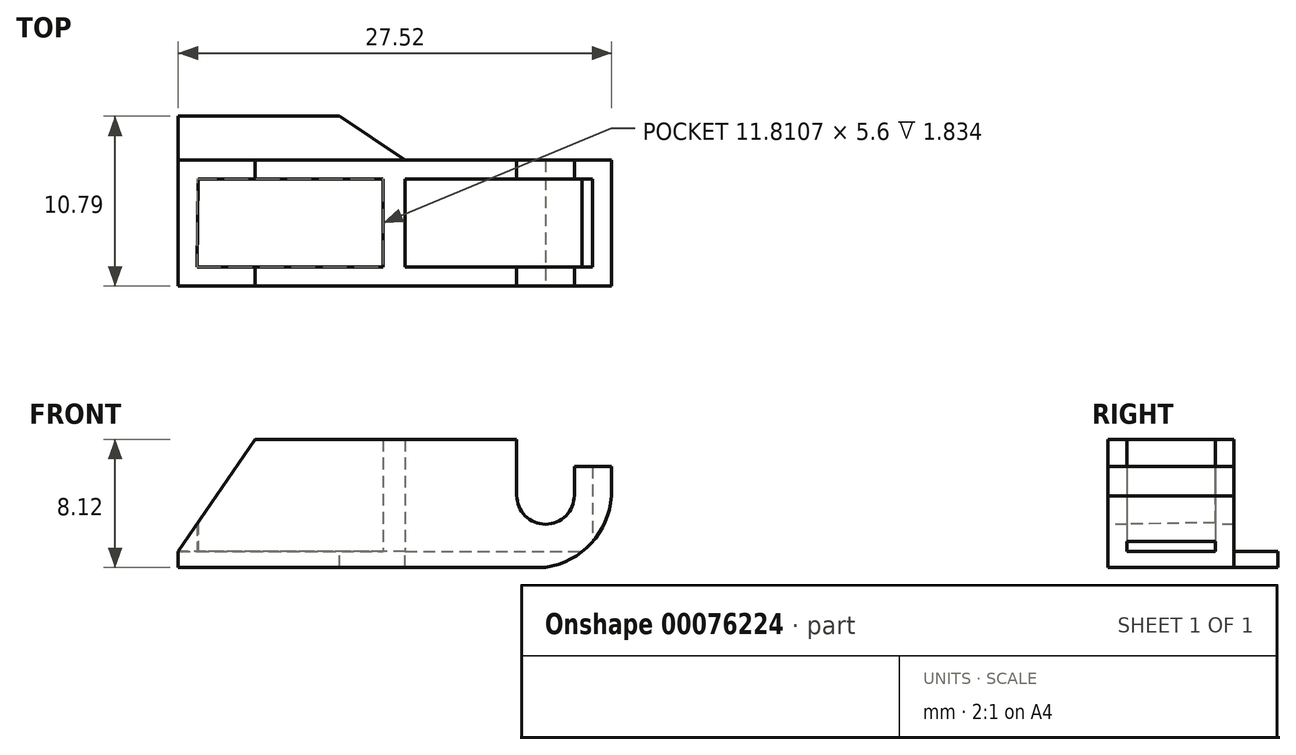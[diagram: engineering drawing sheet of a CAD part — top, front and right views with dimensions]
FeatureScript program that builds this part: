
annotation { "Feature Type Name" : "Feature", "Feature Type Description" : "" }
export const myFeature = defineFeature(function(context is Context, id is Id, definition is map)
    precondition{}
    {
        {
            var Q0;
            Q0=qCreatedBy(makeId("Top.planeOp"),FACE);
            var sketch = newSketch(context, id + "F0", { "sketchPlane" : qUnion([Q0])});
            skLineSegment(sketch, "E0", {"start": v(0, 0) * mm, "end": v(0, 10.79) * mm});
            skLineSegment(sketch, "E1", {"start": v(0, 10.79) * mm, "end": v(10.26, 10.79) * mm});
            skLineSegment(sketch, "E2", {"start": v(0, 0) * mm, "end": v(10.26, 0) * mm});
            skLineSegment(sketch, "E3", {"start": v(10.26, 0) * mm, "end": v(14.42, 0) * mm});
            skLineSegment(sketch, "E4", {"start": v(14.42, 0) * mm, "end": v(22.52, 0) * mm});
            skLineSegment(sketch, "E5", {"start": v(22.52, 0) * mm, "end": v(27.52, 0) * mm});
            skLineSegment(sketch, "E6", {"start": v(27.52, 0) * mm, "end": v(27.52, 8) * mm});
            skLineSegment(sketch, "E7", {"start": v(27.52, 8) * mm, "end": v(22.52, 8) * mm});
            skLineSegment(sketch, "E8", {"start": v(22.52, 8) * mm, "end": v(14.42, 8) * mm});
            skLineSegment(sketch, "E9", {"start": v(14.42, 8) * mm, "end": v(10.26, 10.79) * mm});
            skLineSegment(sketch, "E10.0", {"start": v(1.2, 1.2) * mm, "end": v(1.26, 6.8) * mm});
            skLineSegment(sketch, "E10.1", {"start": v(1.2, 1.2) * mm, "end": v(10.26, 1.2) * mm});
            skLineSegment(sketch, "E10.3", {"start": v(10.26, 1.2) * mm, "end": v(14.42, 1.2) * mm});
            skLineSegment(sketch, "E10.4", {"start": v(14.42, 1.2) * mm, "end": v(22.52, 1.2) * mm});
            skLineSegment(sketch, "E10.5", {"start": v(22.52, 1.2) * mm, "end": v(26.32, 1.2) * mm});
            skLineSegment(sketch, "E10.7", {"start": v(22.52, 6.8) * mm, "end": v(14.05, 6.8) * mm});
            skLineSegment(sketch, "E10.8", {"start": v(26.32, 6.8) * mm, "end": v(22.52, 6.8) * mm});
            skLineSegment(sketch, "E10.9", {"start": v(26.32, 1.2) * mm, "end": v(26.32, 6.8) * mm});
            skLineSegment(sketch, "E11", {"start": v(14.05, 6.8) * mm, "end": v(1.26, 6.8) * mm});
            skLineSegment(sketch, "E12", {"start": v(14.42, 8) * mm, "end": v(1.26, 8) * mm});
            skLineSegment(sketch, "E13", {"start": v(1.26, 8) * mm, "end": v(0, 8) * mm});
            skLineSegment(sketch, "E14", {"start": v(14.42, 1.2) * mm, "end": v(14.42, 6.8) * mm});
            skLineSegment(sketch, "E15", {"start": v(14.42, 6.8) * mm, "end": v(13.01, 6.8) * mm});
            skLineSegment(sketch, "E16", {"start": v(13.01, 6.8) * mm, "end": v(13.01, 1.2) * mm});
            skLineSegment(sketch, "E17", {"start": v(13.01, 1.2) * mm, "end": v(14.42, 1.2) * mm});
            skSolve(sketch);
        }
        {
            var Q0;
            {var subQ1=sQuery(id+"F0.wireOp",EDGE,"E2");Q0=makeQuery(id+"F0.imprint","IMPRINT",FACE,{"disambiguationData":[TD([[makeQuery(id+"F0.imprint","IMPRINT",EDGE,{"derivedFrom":subQ1}),1.0]])]});}
            var Q1;
            {var subQ3=sQuery(id+"F0.wireOp",EDGE,"E14");Q1=makeQuery(id+"F0.imprint","IMPRINT",FACE,{"disambiguationData":[TD([[makeQuery(id+"F0.imprint","IMPRINT",EDGE,{"derivedFrom":subQ3}),1.0]])]});}
            extrude(context, id + "F1", {"entities" : qUnion([Q0, Q1]), "depth" : 7.12 * mm});
        }
        {
            var Q0;
            {var subQ0=sQuery(id+"F0.wireOp",EDGE,"E1");Q0=makeQuery(id+"F0.imprint","IMPRINT",FACE,{"disambiguationData":[TD([[makeQuery(id+"F0.imprint","IMPRINT",EDGE,{"derivedFrom":subQ0}),-1.0]])]});}
            var Q1;
            {var subQ1=sQuery(id+"F0.wireOp",EDGE,"E2");Q1=makeQuery(id+"F0.imprint","IMPRINT",FACE,{"disambiguationData":[TD([[makeQuery(id+"F0.imprint","IMPRINT",EDGE,{"derivedFrom":subQ1}),1.0]])]});}
            var Q2;
            Q2=makeQuery(id+"F0.imprint","IMPRINT",FACE,{"disambiguationData":[TD([[makeQuery(id+"F0.imprint","IMPRINT",EDGE,{"derivedFrom":sQuery(id+"F0.wireOp",EDGE,"E10.0")}),-1.0]])]});
            var Q3;
            {var subQ3=sQuery(id+"F0.wireOp",EDGE,"E14");Q3=makeQuery(id+"F0.imprint","IMPRINT",FACE,{"disambiguationData":[TD([[makeQuery(id+"F0.imprint","IMPRINT",EDGE,{"derivedFrom":subQ3}),1.0]])]});}
            var Q4;
            Q4=makeQuery(id+"F0.imprint","IMPRINT",FACE,{"disambiguationData":[TD([[makeQuery(id+"F0.imprint","IMPRINT",EDGE,{"derivedFrom":sQuery(id+"F0.wireOp",EDGE,"E10.4")}),1.0]])]});
            extrude(context, id + "F2", {"entities" : qUnion([Q0, Q1, Q2, Q3, Q4]), "operationType" : NewBodyOperationType.ADD, "oppositeDirection" : true, "depth" : 1 * mm});
        }
        {
            var Q0;
            Q0=qCreatedBy(makeId("Front.planeOp"),FACE);
            var sketch = newSketch(context, id + "F3", { "sketchPlane" : qUnion([Q0])});
            skLineSegment(sketch, "E18", {"start": v(23.33, -0.09) * mm, "end": v(23.33, 3.57) * mm, "construction": true});
            skCircle(sketch, "E19", {"center": v(23.33, 3.57) * mm, "radius": 1.83 * mm});
            skLineSegment(sketch, "E20", {"start": v(0, 0) * mm, "end": v(4.88, 7.12) * mm});
            skLineSegment(sketch, "E21", {"start": v(0, 0) * mm, "end": v(0, 7.12) * mm});
            skLineSegment(sketch, "E22", {"start": v(0, 7.12) * mm, "end": v(4.88, 7.12) * mm});
            skLineSegment(sketch, "E23.0", {"start": v(0, 7.12) * mm, "end": v(27.52, 7.12) * mm});
            skLineSegment(sketch, "E24", {"start": v(21.5, 3.57) * mm, "end": v(21.5, 7.12) * mm});
            skLineSegment(sketch, "E25", {"start": v(25.16, 3.57) * mm, "end": v(25.16, 7.12) * mm});
            skLineSegment(sketch, "E26", {"start": v(25.16, 7.12) * mm, "end": v(21.5, 7.12) * mm});
            skLineSegment(sketch, "E27.0", {"start": v(27.52, 7.12) * mm, "end": v(27.52, -1) * mm});
            skLineSegment(sketch, "E28", {"start": v(23.33, 5.4) * mm, "end": v(27.52, 5.4) * mm});
            skLineSegment(sketch, "E29.0", {"start": v(0, -1) * mm, "end": v(27.52, -1) * mm});
            skPoint(sketch, "E30.endSnap0", {"position": v(23.33, 1.74) * mm});
            skArc(sketch, "E31", {"start": v(23.33, -1) * mm, "mid": v(26.22, 0.53) * mm, "end": v(27.52, 3.53) * mm});
            skSolve(sketch);
        }
        {
            var Q0;
            Q0=makeQuery(id+"F3.imprint","IMPRINT",FACE,{"disambiguationData":[TD([[makeQuery(id+"F3.imprint","IMPRINT",EDGE,{"derivedFrom":sQuery(id+"F3.wireOp",EDGE,"E19")}),1.0]])]});
            var Q1;
            {var subQ0=sQuery(id+"F3.wireOp",EDGE,"E24");Q1=makeQuery(id+"F3.imprint","IMPRINT",FACE,{"disambiguationData":[TD([[makeQuery(id+"F3.imprint","IMPRINT",EDGE,{"derivedFrom":subQ0}),-1.0]])]});}
            var Q2;
            {var subQ0=sQuery(id+"F3.wireOp",EDGE,"E27.0");var subQ1=sQuery(id+"F3.wireOp",EDGE,"E23.0");var subQ2=makeQuery(id+"F3.imprint","INTERSECT",VERTEX,{"derivedFrom":[subQ1,subQ0]});Q2=makeQuery(id+"F3.imprint","IMPRINT",FACE,{"disambiguationData":[TD([[makeQuery(id+"F3.imprint","IMPRINT",EDGE,{"disambiguationData":[TD([[subQ2,-1.0]])],"derivedFrom":subQ0}),-1.0]])]});}
            var Q3;
            {var subQ0=sQuery(id+"F3.wireOp",EDGE,"E25");var subQ1=sQuery(id+"F3.wireOp",EDGE,"E19");var subQ2=makeQuery(id+"F3.imprint","INTERSECT",VERTEX,{"derivedFrom":[subQ1,subQ0]});Q3=makeQuery(id+"F3.imprint","IMPRINT",FACE,{"disambiguationData":[TD([[makeQuery(id+"F3.imprint","IMPRINT",EDGE,{"disambiguationData":[TD([[subQ2,-1.0]])],"derivedFrom":subQ1}),-1.0]])]});}
            var Q4;
            {var subQ3=sQuery(id+"F3.wireOp",EDGE,"E31");Q4=makeQuery(id+"F3.imprint","IMPRINT",FACE,{"disambiguationData":[TD([[makeQuery(id+"F3.imprint","IMPRINT",EDGE,{"derivedFrom":subQ3}),-1.0]])]});}
            var Q5;
            Q5=makeQuery(id+"F1.opExtrude","SWEPT_FACE",FACE,{"disambiguationData":[OSD([sQuery(id+"F0.wireOp",EDGE,"E10.7"),sQuery(id+"F0.wireOp",EDGE,"E10.8")])]});
            extrude(context, id + "F4", {"entities" : qUnion([Q0, Q1, Q2, Q3, Q4]), "operationType" : NewBodyOperationType.REMOVE, "endBound" : BoundingType.THROUGH_ALL, "oppositeDirection" : true, "endBoundEntityFace" : qUnion([Q5]), "depth" : 25 * mm});
        }
        {
            var Q0;
            Q0=makeQuery(id+"F3.imprint","IMPRINT",FACE,{"disambiguationData":[TD([[makeQuery(id+"F3.imprint","IMPRINT",EDGE,{"derivedFrom":sQuery(id+"F3.wireOp",EDGE,"E20")}),1.0]])]});
            extrude(context, id + "F5", {"entities" : qUnion([Q0]), "operationType" : NewBodyOperationType.REMOVE, "oppositeDirection" : true, "depth" : 25 * mm});
        }
    });
